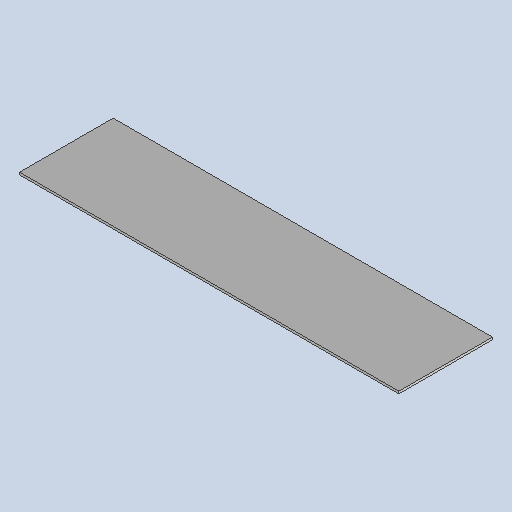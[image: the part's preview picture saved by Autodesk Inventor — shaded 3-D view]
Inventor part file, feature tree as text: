
AUTODESK INVENTOR PART (.ipt)
format: ipt  version: 2025 (Build 290162010, 162A)  size: 252,928 bytes
history: native  units: mm
features: other x4, sketch x2, sheet_metal_op x1
ambient origin geometry x8: Origin, YZ Plane, XZ Plane, XY Plane, X Axis, Y Axis, Z Axis, Center Point
bodies: Solid1 (feature_tree)
feature tree (7):
  sheet_metal_op  "Face1"
  other  "Mark1"
  other  "A-Side Definition"
  sketch  "Sketch1"  dims[d0=486.0mm]
  other  "Plate1"
  sketch  "Sketch2"  dims[d1=120.0mm d2=3.0mm d6=200.0mm d9=20.0mm d10=20.0mm d11=20.0mm]
  other  "Definition1"
